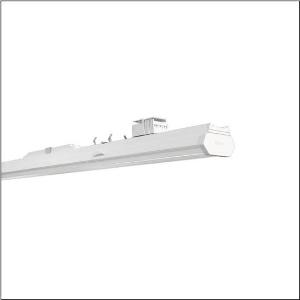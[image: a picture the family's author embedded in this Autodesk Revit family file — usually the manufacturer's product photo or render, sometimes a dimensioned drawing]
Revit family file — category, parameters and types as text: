
# Revit family: licross_r__21_protected_mo_52td11mn4a5g_25e5
name_source: partatom
category: Lighting Fixtures
units: mm (PartAtom-declared; Revit-internal decimal feet)

## family parameters
Cut with Voids When Loaded = No
Host = Face
Light Source = No
Part Type = Normal
Room Calculation Point = No
Round Connector Dimension = Use Diameter
Shared = No

## types (1)
- --- (1 x LED, 10700 lm, 60.5 W, 4000K)
    Apparent Load = 61 VA
    CIE Flux Codes = 83 94 98 100 100
    Color Rendering = 80
    Color Temperature = 4000K
    Default Elevation = 1800 mm
    Description = Licross® 21 Protected MO, luminaire insert, of sheet steel, galvanised, coil coated, white, length: 1.500mm, width: 66mm, height: 67mm, LED rated luminous flux: 10.700lm, light colour: 840, control gear: ON/OFF Multilumen, with plug, 3-pole, with phase selection, mains connection: 220..240V, AC, 50/60Hz, rated input power: 61W, halogen-free wiring, primary light control with lens, of plastic, primary optical cover: cover, of PMMA, light emission: direct distribution, primary light characteristic: symmetric, protection rating (complete): IP54, insulation class (complete): insulation class I (protective earthing), certification: CE, ENEC, VDE, UKCA, protection symbol: D if used in an environment with non-conductive dust loads with corresponding accessories, impact resistance: IK06, permissible ambient temperature for indoor applications: -35..+45°C, corresponds to IFS (International Featured Standards) requirements for safety and quality in the food industry, reducing of maximum allowable ambient temperature of 5°C with ceiling mounting, LABS conformity tested according to VDMA 24364:2018-05, packaging unit: 1 piece
    Height = 92 mm
    Lamp = 1 x LED
    Lamp Light Flux = 10700 lm
    Lamp Power = 60.5 W
    Lamp count = 1
    Length = 1500 mm
    Luminous efficacy = 177 lm/W
    Manufacturer = Siteco
    ModVariant = No
    Model = 52TD11MN4A5G
    Mounting Place = Ceiling
    Mounting Type = Pendant
    Number of Poles = 1
    OnlyDefault = Yes
    Power Factor = 1
    Product Name = Licross® 21 Protected MO
    Product group = luminaire insert
    ProductGroupID = 901
    Protection Class = Protection class I
    Protection Degree = IP 54
    RLX_Detail_Level = 1
    RLX_Emergency_Light_Flux = 0 lm
    RLX_Emergency_Type = 0
    RLX_Emergency_Type_DB = No
    RlxData = <blob elided: 21833 chars, md5=fa631bf2>
    Socket = socket
    Standby Power = 0 W
    System Light Flux = 10700 lm
    System Power = 61 W
    Type Comments = factory setting: luminous flux: 100 % | (A | C | E) | 140 mA
    Type Image = l_1256148.jpg
    URL = http://relux.com
    VarID = @adj_039205
    Voltage = 0 V
    Weight = 0.00 kg
    Width = 88 mm

## geometry (parser evidence)
native form markers: Blend x4, Sweep x12
no freeform markers — native parametric forms only
